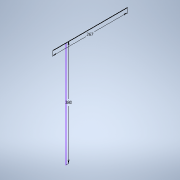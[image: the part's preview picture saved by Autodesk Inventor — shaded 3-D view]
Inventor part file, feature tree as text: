
AUTODESK INVENTOR PART (.ipt)
format: ipt  version: 2020 (Build 240168000, 168)  size: 83,456 bytes
history: native  units: in
note: dims shown in document units (in); Inventor stores cm internally (conversion verified against a paired STEP export)
features: sketch x1
ambient origin geometry x8: Origin, YZ Plane, XZ Plane, XY Plane, X Axis, Y Axis, Z Axis, Center Point
feature tree (1):
  sketch  "Sketch1"
